# Revit family: Font_Easy_Chair_Offecct
name_source: partatom
category: Furniture
revit_build: Autodesk Revit 2018 (Build: 20170223_1515(x64)
units: mm (PartAtom-declared; Revit-internal decimal feet)

## family parameters
Always vertical = Yes
Cut with Voids When Loaded = No
OmniClass Number = 23.40.20.14.14.11
OmniClass Title = Chairs
Room Calculation Point = No
Shared = No
Work Plane-Based = No

## types (1)
- Font, Easy Chair
    ArmchairMainMaterial = Kvadrat Halligndal Blue 754
    ArmchairSecondaryMaterial = Dark blue steel
    AssetType = Movable
    BIMObjectName = Font_Easy_Chair_Offecct
    Brand = Offecct
    Category = Easy Chairs
    Color = Multiple
    ConvergoRefNr = 0019-2101-0005-SE
    Cost = 0 $
    Designer = Matti Klenell
    HighestSeatingHeight = 430 mm  [stored 1.41076 ft]
    IfcExportAs = IfcFurnishingElementType
    IfcExportType = CHAIR
    LowestSeatingHeight = 372 mm
    Manufacturer = Offecct
    ManufacturerName = Offecct
    ManufacturerURL = https://www.offecct.com
    Material = Steel&Fabric
    Model = Font, Easy Chair
    ModelNumber = 10126
    Name = Font_Easy_Chair
    NominalDepth = 770 mm
    NominalHeight = 760 mm
    NominalLength = 880 mm
    SeatingHeight = 430 mm  [stored 1.41076 ft]
    Size = 880x770x760 mm
    Uniclass2 = Pr_40_50_12_48
    Uniclass2015Description = Easy chairs
    Uniclass2015Reference = Pr_40_50_12_26
    Version = 1
    VersionDate = 21/01/2021

note: [stored X ft] marks values corroborated as IEEE doubles in the binary element streams (Revit-internal decimal feet)

## geometry (parser evidence)
native form markers: Sweep x16
no freeform markers — native parametric forms only
